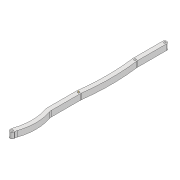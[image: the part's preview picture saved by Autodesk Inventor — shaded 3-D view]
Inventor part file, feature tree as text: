
AUTODESK INVENTOR PART (.ipt)
format: ipt  version: 2022 (Build 260153000, 153)  size: 131,072 bytes
history: native  units: mm
features: extrude x1, other x1, fillet x1, sketch x1
ambient origin geometry x8: Origin, YZ Plane, XZ Plane, XY Plane, X Axis, Y Axis, Z Axis, Center Point
bodies: Solid1 (feature_tree)
feature tree (4):
  extrude  "Extrusion1"  Depth=6.0mm
  other  "Work Axis1"
  fillet  "Fillet1"  Radius=3.0mm
  sketch  "Sketch1"  dims[d0=212.9mm d1=6.0mm d2=3.0mm d3=3.0mm d4=8.0mm d5=0.0mm d6=3.0mm d7=171.332mm d8=3.0mm d9=92.628mm d10=300.0mm d11=300.0mm d14=2.0mm d15=50.0mm d16=70.0mm d17=70.0mm d18=10.0mm]
